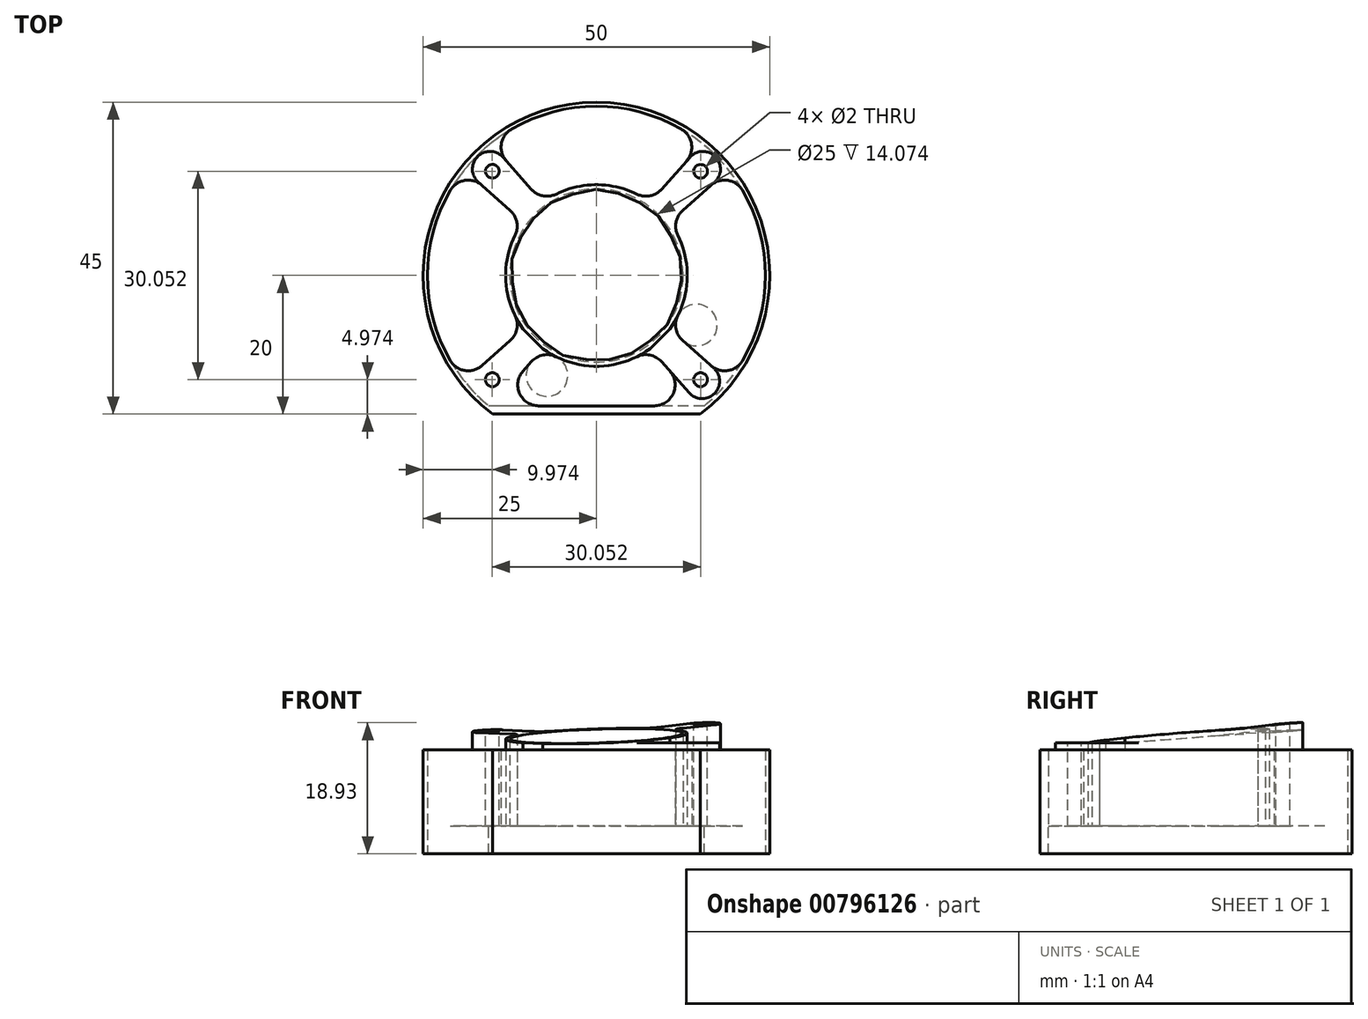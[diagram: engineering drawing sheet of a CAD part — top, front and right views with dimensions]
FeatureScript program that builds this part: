
annotation { "Feature Type Name" : "Feature", "Feature Type Description" : "" }
export const myFeature = defineFeature(function(context is Context, id is Id, definition is map)
    precondition{}
    {
        {
            var Q0;
            Q0=qCreatedBy(makeId("Top.planeOp"),FACE);
            var sketch = newSketch(context, id + "F0", { "sketchPlane" : qUnion([Q0])});
            skLineSegment(sketch, "E0", {"start": v(0, 25) * mm, "end": v(0, -20) * mm, "construction": true});
            skLineSegment(sketch, "E1", {"start": v(0, -20) * mm, "end": v(-15, -20) * mm});
            skLineSegment(sketch, "E2", {"start": v(0, -20) * mm, "end": v(15, -20) * mm});
            skArc(sketch, "E3", {"start": v(-15, -20) * mm, "mid": v(0, -25) * mm, "end": v(15, -20) * mm, "construction": true});
            skArc(sketch, "E4", {"start": v(15, -20) * mm, "mid": v(0, 25) * mm, "end": v(-15, -20) * mm});
            skCircle(sketch, "E5", {"center": v(0, 0) * mm, "radius": 12.5 * mm});
            skCircle(sketch, "E6", {"center": v(0, 0) * mm, "radius": 13.1 * mm});
            skArc(sketch, "E7", {"start": v(13.98, -20) * mm, "mid": v(0, 24.4) * mm, "end": v(-13.98, -20) * mm});
            skArc(sketch, "E8", {"start": v(-13.98, -20) * mm, "mid": v(0, -24.4) * mm, "end": v(13.98, -20) * mm, "construction": true});
            skLineSegment(sketch, "E9", {"start": v(0, -20) * mm, "end": v(0, -18.8) * mm});
            skLineSegment(sketch, "E10", {"start": v(0, -18.8) * mm, "end": v(-15.55, -18.8) * mm});
            skLineSegment(sketch, "E11", {"start": v(0, -18.8) * mm, "end": v(15.55, -18.8) * mm});
            skSolve(sketch);
        }
        {
            var Q0;
            {var subQ0=sQuery(id+"F0.wireOp",EDGE,"E4");Q0=makeQuery(id+"F0.imprint","IMPRINT",FACE,{"disambiguationData":[TD([[makeQuery(id+"F0.imprint","IMPRINT",EDGE,{"derivedFrom":subQ0}),1.0]])]});}
            var Q1;
            Q1=makeQuery(id+"F0.imprint","IMPRINT",FACE,{"disambiguationData":[TD([[makeQuery(id+"F0.imprint","IMPRINT",EDGE,{"derivedFrom":sQuery(id+"F0.wireOp",EDGE,"E5")}),-1.0]])]});
            var Q2;
            {var subQ0=sQuery(id+"F0.wireOp",EDGE,"E9");Q2=makeQuery(id+"F0.imprint","IMPRINT",FACE,{"disambiguationData":[TD([[makeQuery(id+"F0.imprint","IMPRINT",EDGE,{"derivedFrom":subQ0}),1.0]])]});}
            var Q3;
            {var subQ0=sQuery(id+"F0.wireOp",EDGE,"E9");Q3=makeQuery(id+"F0.imprint","IMPRINT",FACE,{"disambiguationData":[TD([[makeQuery(id+"F0.imprint","IMPRINT",EDGE,{"derivedFrom":subQ0}),-1.0]])]});}
            extrude(context, id + "F1", {"entities" : qUnion([Q0, Q1, Q2, Q3]), "depth" : 8 * mm, "offsetDistance" : 25 * mm});
        }
        {
            var Q0;
            Q0=makeQuery(id+"F1.opExtrude","CAP_FACE",FACE,{"disambiguationData":[OSD([sQuery(id+"F0.wireOp",EDGE,"E1"),sQuery(id+"F0.wireOp",EDGE,"E2"),sQuery(id+"F0.wireOp",EDGE,"E4"),sQuery(id+"F0.wireOp",EDGE,"E7"),sQuery(id+"F0.wireOp",EDGE,"E10"),sQuery(id+"F0.wireOp",EDGE,"E11")])],"isStart":false});
            var sketch = newSketch(context, id + "F2", { "sketchPlane" : qUnion([Q0])});
            skCircle(sketch, "E12", {"center": v(0, 0) * mm, "radius": 21.25 * mm, "construction": true});
            skLineSegment(sketch, "E13", {"start": v(0, 0) * mm, "end": v(0, 21.25) * mm, "construction": true});
            skLineSegment(sketch, "E14", {"start": v(0, 0) * mm, "end": v(15.03, 15.03) * mm, "construction": true});
            skCircle(sketch, "E15", {"center": v(15.03, 15.03) * mm, "radius": 1 * mm});
            skCircle(sketch, "E16", {"center": v(15.03, 15.03) * mm, "radius": 2.5 * mm});
            skLineSegment(sketch, "E17", {"start": v(13.16, 16.69) * mm, "end": v(7.73, 10.58) * mm});
            skLineSegment(sketch, "E18", {"start": v(16.69, 13.16) * mm, "end": v(10.58, 7.73) * mm});
            skLineSegment(sketch, "E19", {"start": v(13.16, 16.69) * mm, "end": v(15.25, 19.04) * mm});
            skLineSegment(sketch, "E20", {"start": v(16.69, 13.16) * mm, "end": v(19.04, 15.25) * mm});
            skLineSegment(sketch, "E21", {"start": v(7.73, 10.58) * mm, "end": v(10.58, 7.73) * mm});
            skSolve(sketch);
        }
        {
            var Q0;
            Q0=makeQuery(id+"F2.imprint","IMPRINT",FACE,{"disambiguationData":[TD([[makeQuery(id+"F2.imprint","IMPRINT",EDGE,{"derivedFrom":sQuery(id+"F2.wireOp",EDGE,"E15")}),-1.0]])]});
            var Q1;
            {var subQ0=sQuery(id+"F2.wireOp",EDGE,"E19");Q1=makeQuery(id+"F2.imprint","IMPRINT",FACE,{"disambiguationData":[TD([[makeQuery(id+"F2.imprint","IMPRINT",EDGE,{"derivedFrom":subQ0}),-1.0]])]});}
            var Q2;
            {var subQ0=sQuery(id+"F2.wireOp",EDGE,"E17");Q2=makeQuery(id+"F2.imprint","IMPRINT",FACE,{"disambiguationData":[TD([[makeQuery(id+"F2.imprint","IMPRINT",EDGE,{"derivedFrom":subQ0}),1.0]])]});}
            extrude(context, id + "F3", {"entities" : qUnion([Q0, Q1, Q2]), "oppositeDirection" : true, "depth" : 8 * mm, "offsetDistance" : 25 * mm});
        }
        {
            var Q0;
            Q0=makeQuery(id+"F3.opExtrude","SWEPT_BODY",BODY,{"disambiguationData":[OSD([sQuery(id+"F0.wireOp",EDGE,"E7"),sQuery(id+"F2.wireOp",EDGE,"E15"),sQuery(id+"F2.wireOp",EDGE,"E17"),sQuery(id+"F2.wireOp",EDGE,"E18"),sQuery(id+"F2.wireOp",EDGE,"E19"),sQuery(id+"F2.wireOp",EDGE,"E20"),sQuery(id+"F2.wireOp",EDGE,"E21")])]});
            var Q1;
            Q1=makeQuery(id+"F1.opExtrude","CAP_EDGE",EDGE,{"disambiguationData":[OSD([sQuery(id+"F0.wireOp",EDGE,"E6")])],"isStart":false});
            circularPattern(context, id + "F4", {"entities" : qUnion([Q0]), "axis" : qUnion([Q1]), "angle" : 360 * degree, "instanceCount" : 4, "equalSpace" : true});
        }
        {
            var Q0;
            Q0=makeQuery(id+"F1.opExtrude","CAP_FACE",FACE,{"disambiguationData":[OSD([sQuery(id+"F0.wireOp",EDGE,"E1"),sQuery(id+"F0.wireOp",EDGE,"E2"),sQuery(id+"F0.wireOp",EDGE,"E4"),sQuery(id+"F0.wireOp",EDGE,"E7"),sQuery(id+"F0.wireOp",EDGE,"E10"),sQuery(id+"F0.wireOp",EDGE,"E11")])],"isStart":true});
            extrude(context, id + "F5", {"entities" : qUnion([Q0]), "operationType" : NewBodyOperationType.ADD, "depth" : 4 * mm, "offsetDistance" : 25 * mm});
        }
        {
            var Q0;
            Q0=makeQuery(id+"F1.opExtrude","SWEPT_BODY",BODY,{"disambiguationData":[OSD([sQuery(id+"F0.wireOp",EDGE,"E1"),sQuery(id+"F0.wireOp",EDGE,"E2"),sQuery(id+"F0.wireOp",EDGE,"E4"),sQuery(id+"F0.wireOp",EDGE,"E7"),sQuery(id+"F0.wireOp",EDGE,"E10"),sQuery(id+"F0.wireOp",EDGE,"E11")])]});
            var Q1;
            Q1=makeQuery(id+"F1.opExtrude","SWEPT_BODY",BODY,{"disambiguationData":[OSD([sQuery(id+"F0.wireOp",EDGE,"E5"),sQuery(id+"F0.wireOp",EDGE,"E6")])]});
            booleanBodies(context, id + "F6", {"operationType" : BooleanOperationType.UNION, "tools" : qUnion([Q0, Q1])});
        }
        {
            var Q0;
            {var subQ0=sQuery(id+"F0.wireOp",EDGE,"E7");var subQ1=makeQuery(id+"F3.opExtrude","CAP_FACE",FACE,{"disambiguationData":[OSD([subQ0,sQuery(id+"F2.wireOp",EDGE,"E15"),sQuery(id+"F2.wireOp",EDGE,"E17"),sQuery(id+"F2.wireOp",EDGE,"E18"),sQuery(id+"F2.wireOp",EDGE,"E19"),sQuery(id+"F2.wireOp",EDGE,"E20"),sQuery(id+"F2.wireOp",EDGE,"E21")])],"isStart":true});Q0=makeQuery(id+"F6.opBoolean","MERGE",FACE,{"derivedFrom":[makeQuery(id+"F1.opExtrude","CAP_FACE",FACE,{"disambiguationData":[OSD([sQuery(id+"F0.wireOp",EDGE,"E5"),sQuery(id+"F0.wireOp",EDGE,"E6")])],"isStart":false}),makeQuery(id+"F5.boolean.opBoolean","MERGE",FACE,{"derivedFrom":[makeQuery(id+"F1.opExtrude","CAP_FACE",FACE,{"disambiguationData":[OSD([sQuery(id+"F0.wireOp",EDGE,"E1"),sQuery(id+"F0.wireOp",EDGE,"E2"),sQuery(id+"F0.wireOp",EDGE,"E4"),subQ0,sQuery(id+"F0.wireOp",EDGE,"E10"),sQuery(id+"F0.wireOp",EDGE,"E11")])],"isStart":false}),subQ1,makeQuery(id+"F4.opPattern","COPY",FACE,{"derivedFrom":subQ1,"instanceName":"1"}),makeQuery(id+"F4.opPattern","COPY",FACE,{"derivedFrom":subQ1,"instanceName":"2"}),makeQuery(id+"F4.opPattern","COPY",FACE,{"derivedFrom":subQ1,"instanceName":"3"})]})]});}
            var sketch = newSketch(context, id + "F7", { "sketchPlane" : qUnion([Q0])});
            skLineSegment(sketch, "E22", {"start": v(15.25, 19.04) * mm, "end": v(19.04, 15.25) * mm});
            skLineSegment(sketch, "E23", {"start": v(19.04, 15.25) * mm, "end": v(10.58, 7.73) * mm});
            skLineSegment(sketch, "E24", {"start": v(10.58, 7.73) * mm, "end": v(7.73, 10.58) * mm});
            skLineSegment(sketch, "E25", {"start": v(7.73, 10.58) * mm, "end": v(15.25, 19.04) * mm});
            skCircle(sketch, "E26", {"center": v(15.03, 15.03) * mm, "radius": 2.5 * mm});
            skSolve(sketch);
        }
        {
            var Q0;
            {var subQ0=sQuery(id+"F7.wireOp",EDGE,"E24");Q0=makeQuery(id+"F7.imprint","IMPRINT",FACE,{"disambiguationData":[TD([[makeQuery(id+"F7.imprint","IMPRINT",EDGE,{"derivedFrom":subQ0}),-1.0]])]});}
            var Q1;
            {var subQ0=sQuery(id+"F7.wireOp",EDGE,"E22");Q1=makeQuery(id+"F7.imprint","IMPRINT",FACE,{"disambiguationData":[TD([[makeQuery(id+"F7.imprint","IMPRINT",EDGE,{"derivedFrom":subQ0}),-1.0]])]});}
            var Q2;
            Q2=makeQuery(id+"F7.imprint","IMPRINT",FACE,{"disambiguationData":[TD([[makeQuery(id+"F7.imprint","IMPRINT",EDGE,{"derivedFrom":makeQuery(id+"F3.opExtrude","CAP_EDGE",EDGE,{"disambiguationData":[OSD([sQuery(id+"F2.wireOp",EDGE,"E15")])],"isStart":true})}),-1.0]])]});
            extrude(context, id + "F8", {"entities" : qUnion([Q0, Q1, Q2]), "operationType" : NewBodyOperationType.ADD, "depth" : 7 * mm, "offsetDistance" : 25 * mm});
        }
        {
            var Q0;
            {var subQ0=sQuery(id+"F0.wireOp",EDGE,"E7");var subQ1=makeQuery(id+"F3.opExtrude","CAP_FACE",FACE,{"disambiguationData":[OSD([subQ0,sQuery(id+"F2.wireOp",EDGE,"E15"),sQuery(id+"F2.wireOp",EDGE,"E17"),sQuery(id+"F2.wireOp",EDGE,"E18"),sQuery(id+"F2.wireOp",EDGE,"E19"),sQuery(id+"F2.wireOp",EDGE,"E20"),sQuery(id+"F2.wireOp",EDGE,"E21")])],"isStart":true});Q0=makeQuery(id+"F6.opBoolean","MERGE",FACE,{"derivedFrom":[makeQuery(id+"F1.opExtrude","CAP_FACE",FACE,{"disambiguationData":[OSD([sQuery(id+"F0.wireOp",EDGE,"E5"),sQuery(id+"F0.wireOp",EDGE,"E6")])],"isStart":false}),makeQuery(id+"F5.boolean.opBoolean","MERGE",FACE,{"derivedFrom":[makeQuery(id+"F1.opExtrude","CAP_FACE",FACE,{"disambiguationData":[OSD([sQuery(id+"F0.wireOp",EDGE,"E1"),sQuery(id+"F0.wireOp",EDGE,"E2"),sQuery(id+"F0.wireOp",EDGE,"E4"),subQ0,sQuery(id+"F0.wireOp",EDGE,"E10"),sQuery(id+"F0.wireOp",EDGE,"E11")])],"isStart":false}),subQ1,makeQuery(id+"F4.opPattern","COPY",FACE,{"derivedFrom":subQ1,"instanceName":"1"}),makeQuery(id+"F4.opPattern","COPY",FACE,{"derivedFrom":subQ1,"instanceName":"2"}),makeQuery(id+"F4.opPattern","COPY",FACE,{"derivedFrom":subQ1,"instanceName":"3"})]})]});}
            var sketch = newSketch(context, id + "F9", { "sketchPlane" : qUnion([Q0])});
            skLineSegment(sketch, "E27", {"start": v(-15.25, 19.04) * mm, "end": v(-19.04, 15.25) * mm});
            skLineSegment(sketch, "E28", {"start": v(-19.04, 15.25) * mm, "end": v(-10.58, 7.73) * mm});
            skLineSegment(sketch, "E29", {"start": v(-10.58, 7.73) * mm, "end": v(-7.73, 10.58) * mm});
            skLineSegment(sketch, "E30", {"start": v(-7.73, 10.58) * mm, "end": v(-15.25, 19.04) * mm});
            skSolve(sketch);
        }
        {
            var Q0;
            Q0=makeQuery(id+"F9.imprint","IMPRINT",FACE,{"disambiguationData":[TD([[makeQuery(id+"F9.imprint","IMPRINT",EDGE,{"derivedFrom":sQuery(id+"F9.wireOp",EDGE,"E27")}),1.0]])]});
            extrude(context, id + "F10", {"entities" : qUnion([Q0]), "operationType" : NewBodyOperationType.ADD, "depth" : 6 * mm, "offsetDistance" : 25 * mm});
        }
        {
            var Q0;
            {var subQ0=sQuery(id+"F0.wireOp",EDGE,"E7");var subQ1=makeQuery(id+"F3.opExtrude","CAP_FACE",FACE,{"disambiguationData":[OSD([subQ0,sQuery(id+"F2.wireOp",EDGE,"E15"),sQuery(id+"F2.wireOp",EDGE,"E17"),sQuery(id+"F2.wireOp",EDGE,"E18"),sQuery(id+"F2.wireOp",EDGE,"E19"),sQuery(id+"F2.wireOp",EDGE,"E20"),sQuery(id+"F2.wireOp",EDGE,"E21")])],"isStart":true});Q0=makeQuery(id+"F6.opBoolean","MERGE",FACE,{"derivedFrom":[makeQuery(id+"F1.opExtrude","CAP_FACE",FACE,{"disambiguationData":[OSD([sQuery(id+"F0.wireOp",EDGE,"E5"),sQuery(id+"F0.wireOp",EDGE,"E6")])],"isStart":false}),makeQuery(id+"F5.boolean.opBoolean","MERGE",FACE,{"derivedFrom":[makeQuery(id+"F1.opExtrude","CAP_FACE",FACE,{"disambiguationData":[OSD([sQuery(id+"F0.wireOp",EDGE,"E1"),sQuery(id+"F0.wireOp",EDGE,"E2"),sQuery(id+"F0.wireOp",EDGE,"E4"),subQ0,sQuery(id+"F0.wireOp",EDGE,"E10"),sQuery(id+"F0.wireOp",EDGE,"E11")])],"isStart":false}),subQ1,makeQuery(id+"F4.opPattern","COPY",FACE,{"derivedFrom":subQ1,"instanceName":"1"}),makeQuery(id+"F4.opPattern","COPY",FACE,{"derivedFrom":subQ1,"instanceName":"2"}),makeQuery(id+"F4.opPattern","COPY",FACE,{"derivedFrom":subQ1,"instanceName":"3"})]})]});}
            var sketch = newSketch(context, id + "F11", { "sketchPlane" : qUnion([Q0])});
            skLineSegment(sketch, "E31", {"start": v(-19.04, -15.25) * mm, "end": v(-15.04, -18.8) * mm});
            skLineSegment(sketch, "E32", {"start": v(-15.04, -18.8) * mm, "end": v(-7.73, -10.58) * mm});
            skLineSegment(sketch, "E33", {"start": v(-7.73, -10.58) * mm, "end": v(-10.58, -7.73) * mm});
            skSolve(sketch);
        }
        {
            var Q0;
            Q0=makeQuery(id+"F11.imprint","IMPRINT",FACE,{"disambiguationData":[TD([[makeQuery(id+"F11.imprint","IMPRINT",EDGE,{"derivedFrom":sQuery(id+"F11.wireOp",EDGE,"E31")}),1.0]])]});
            extrude(context, id + "F12", {"entities" : qUnion([Q0]), "operationType" : NewBodyOperationType.ADD, "depth" : 3 * mm, "offsetDistance" : 25 * mm});
        }
        {
            var Q0;
            {var subQ0=sQuery(id+"F0.wireOp",EDGE,"E7");var subQ1=makeQuery(id+"F3.opExtrude","CAP_FACE",FACE,{"disambiguationData":[OSD([subQ0,sQuery(id+"F2.wireOp",EDGE,"E15"),sQuery(id+"F2.wireOp",EDGE,"E17"),sQuery(id+"F2.wireOp",EDGE,"E18"),sQuery(id+"F2.wireOp",EDGE,"E19"),sQuery(id+"F2.wireOp",EDGE,"E20"),sQuery(id+"F2.wireOp",EDGE,"E21")])],"isStart":true});Q0=makeQuery(id+"F6.opBoolean","MERGE",FACE,{"derivedFrom":[makeQuery(id+"F1.opExtrude","CAP_FACE",FACE,{"disambiguationData":[OSD([sQuery(id+"F0.wireOp",EDGE,"E5"),sQuery(id+"F0.wireOp",EDGE,"E6")])],"isStart":false}),makeQuery(id+"F5.boolean.opBoolean","MERGE",FACE,{"derivedFrom":[makeQuery(id+"F1.opExtrude","CAP_FACE",FACE,{"disambiguationData":[OSD([sQuery(id+"F0.wireOp",EDGE,"E1"),sQuery(id+"F0.wireOp",EDGE,"E2"),sQuery(id+"F0.wireOp",EDGE,"E4"),subQ0,sQuery(id+"F0.wireOp",EDGE,"E10"),sQuery(id+"F0.wireOp",EDGE,"E11")])],"isStart":false}),subQ1,makeQuery(id+"F4.opPattern","COPY",FACE,{"derivedFrom":subQ1,"instanceName":"1"}),makeQuery(id+"F4.opPattern","COPY",FACE,{"derivedFrom":subQ1,"instanceName":"2"}),makeQuery(id+"F4.opPattern","COPY",FACE,{"derivedFrom":subQ1,"instanceName":"3"})]})]});}
            var sketch = newSketch(context, id + "F13", { "sketchPlane" : qUnion([Q0])});
            skLineSegment(sketch, "E34", {"start": v(7.73, -10.58) * mm, "end": v(10.58, -7.73) * mm});
            skLineSegment(sketch, "E35", {"start": v(10.58, -7.73) * mm, "end": v(19.04, -15.25) * mm});
            skLineSegment(sketch, "E36", {"start": v(19.04, -15.25) * mm, "end": v(15.04, -18.8) * mm});
            skLineSegment(sketch, "E37", {"start": v(15.04, -18.8) * mm, "end": v(7.73, -10.58) * mm});
            skSolve(sketch);
        }
        {
            var Q0;
            Q0=makeQuery(id+"F13.imprint","IMPRINT",FACE,{"disambiguationData":[TD([[makeQuery(id+"F13.imprint","IMPRINT",EDGE,{"derivedFrom":sQuery(id+"F13.wireOp",EDGE,"E34")}),-1.0]])]});
            extrude(context, id + "F14", {"entities" : qUnion([Q0]), "operationType" : NewBodyOperationType.ADD, "depth" : 4 * mm, "offsetDistance" : 25 * mm});
        }
        {
            var Q0;
            {var subQ0=sQuery(id+"F2.wireOp",EDGE,"E20");var subQ1=sQuery(id+"F2.wireOp",EDGE,"E18");var subQ3=sQuery(id+"F2.wireOp",EDGE,"E19");var subQ4=sQuery(id+"F2.wireOp",EDGE,"E17");var subQ6=sQuery(id+"F0.wireOp",EDGE,"E6");var subQ7=sQuery(id+"F0.wireOp",EDGE,"E5");var subQ8=sQuery(id+"F0.wireOp",EDGE,"E7");var subQ9=makeQuery(id+"F3.opExtrude","CAP_FACE",FACE,{"disambiguationData":[OSD([subQ8,sQuery(id+"F2.wireOp",EDGE,"E15"),subQ4,subQ1,subQ3,subQ0,sQuery(id+"F2.wireOp",EDGE,"E21")])],"isStart":true});Q0=makeQuery(id+"F14.boolean.opBoolean","SPLIT",FACE,{"disambiguationData":[TD([makeQuery(id+"F1.opExtrude","SWEPT_FACE",FACE,{"disambiguationData":[OSD([subQ7])]})])],"derivedFrom":makeQuery(id+"F6.opBoolean","MERGE",FACE,{"derivedFrom":[makeQuery(id+"F1.opExtrude","CAP_FACE",FACE,{"disambiguationData":[OSD([subQ7,subQ6])],"isStart":false}),makeQuery(id+"F5.boolean.opBoolean","MERGE",FACE,{"derivedFrom":[makeQuery(id+"F1.opExtrude","CAP_FACE",FACE,{"disambiguationData":[OSD([sQuery(id+"F0.wireOp",EDGE,"E1"),sQuery(id+"F0.wireOp",EDGE,"E2"),sQuery(id+"F0.wireOp",EDGE,"E4"),subQ8,sQuery(id+"F0.wireOp",EDGE,"E10"),sQuery(id+"F0.wireOp",EDGE,"E11")])],"isStart":false}),subQ9,makeQuery(id+"F4.opPattern","COPY",FACE,{"derivedFrom":subQ9,"instanceName":"1"}),makeQuery(id+"F4.opPattern","COPY",FACE,{"derivedFrom":subQ9,"instanceName":"2"}),makeQuery(id+"F4.opPattern","COPY",FACE,{"derivedFrom":subQ9,"instanceName":"3"})]})]})});}
            extrude(context, id + "F15", {"entities" : qUnion([Q0]), "operationType" : NewBodyOperationType.ADD, "depth" : 7 * mm, "offsetDistance" : 25 * mm});
        }
        {
            var Q0;
            Q0=makeQuery(id+"F8.opExtrude","CAP_VERTEX",VERTEX,{"disambiguationData":[OSD([sQuery(id+"F0.wireOp",EDGE,"E7"),sQuery(id+"F7.wireOp",EDGE,"E22"),sQuery(id+"F7.wireOp",EDGE,"E25")])],"isStart":false});
            var Q1;
            Q1=makeQuery(id+"F14.opExtrude","CAP_VERTEX",VERTEX,{"disambiguationData":[OSD([sQuery(id+"F0.wireOp",EDGE,"E10"),sQuery(id+"F0.wireOp",EDGE,"E11"),sQuery(id+"F13.wireOp",EDGE,"E36"),sQuery(id+"F13.wireOp",EDGE,"E37")])],"isStart":false});
            var Q2;
            Q2=makeQuery(id+"F12.opExtrude","CAP_VERTEX",VERTEX,{"disambiguationData":[OSD([sQuery(id+"F0.wireOp",EDGE,"E10"),sQuery(id+"F0.wireOp",EDGE,"E11"),sQuery(id+"F11.wireOp",EDGE,"E31"),sQuery(id+"F11.wireOp",EDGE,"E32")])],"isStart":false});
            cPlane(context, id + "F16", {"entities" : qUnion([Q0, Q1, Q2]), "cplaneType" : CPlaneType.THREE_POINT, "offset" : 25 * mm, "width" : 150 * mm, "height" : 150 * mm});
        }
        {
            var Q0;
            Q0=qCreatedBy(id+"F16.planeOp",FACE);
            var sketch = newSketch(context, id + "F17", { "sketchPlane" : qUnion([Q0])});
            skLineSegment(sketch, "E38.bottom", {"start": v(-22.72, -24.84) * mm, "end": v(31.37, -24.84) * mm});
            skLineSegment(sketch, "E38.top", {"start": v(-22.72, 19.98) * mm, "end": v(31.37, 19.98) * mm});
            skLineSegment(sketch, "E38.left", {"start": v(-22.72, -24.84) * mm, "end": v(-22.72, 19.98) * mm});
            skLineSegment(sketch, "E38.right", {"start": v(31.37, -24.84) * mm, "end": v(31.37, 19.98) * mm});
            skSolve(sketch);
        }
        {
            var Q0;
            Q0=makeQuery(id+"F17.imprint","IMPRINT",FACE,{"disambiguationData":[TD([[makeQuery(id+"F17.imprint","IMPRINT",EDGE,{"derivedFrom":sQuery(id+"F17.wireOp",EDGE,"E38.bottom")}),1.0]])]});
            extrude(context, id + "F18", {"entities" : qUnion([Q0]), "operationType" : NewBodyOperationType.REMOVE, "depth" : 25 * mm, "offsetDistance" : 25 * mm});
        }
        {
            var Q0;
            {var subQ0=sQuery(id+"F2.wireOp",EDGE,"E20");var subQ1=sQuery(id+"F2.wireOp",EDGE,"E18");var subQ3=sQuery(id+"F0.wireOp",EDGE,"E11");var subQ4=sQuery(id+"F0.wireOp",EDGE,"E10");var subQ5=sQuery(id+"F0.wireOp",EDGE,"E2");var subQ6=sQuery(id+"F0.wireOp",EDGE,"E1");var subQ7=sQuery(id+"F2.wireOp",EDGE,"E19");var subQ8=sQuery(id+"F2.wireOp",EDGE,"E17");var subQ10=sQuery(id+"F0.wireOp",EDGE,"E4");var subQ11=sQuery(id+"F0.wireOp",EDGE,"E7");var subQ12=makeQuery(id+"F3.opExtrude","CAP_FACE",FACE,{"disambiguationData":[OSD([subQ11,sQuery(id+"F2.wireOp",EDGE,"E15"),subQ8,subQ1,subQ7,subQ0,sQuery(id+"F2.wireOp",EDGE,"E21")])],"isStart":true});Q0=makeQuery(id+"F14.boolean.opBoolean","SPLIT",FACE,{"disambiguationData":[TD([makeQuery(id+"F1.opExtrude","SWEPT_FACE",FACE,{"disambiguationData":[OSD([subQ10])]})])],"derivedFrom":makeQuery(id+"F6.opBoolean","MERGE",FACE,{"derivedFrom":[makeQuery(id+"F1.opExtrude","CAP_FACE",FACE,{"disambiguationData":[OSD([sQuery(id+"F0.wireOp",EDGE,"E5"),sQuery(id+"F0.wireOp",EDGE,"E6")])],"isStart":false}),makeQuery(id+"F5.boolean.opBoolean","MERGE",FACE,{"derivedFrom":[makeQuery(id+"F1.opExtrude","CAP_FACE",FACE,{"disambiguationData":[OSD([subQ6,subQ5,subQ10,subQ11,subQ4,subQ3])],"isStart":false}),subQ12,makeQuery(id+"F4.opPattern","COPY",FACE,{"derivedFrom":subQ12,"instanceName":"1"}),makeQuery(id+"F4.opPattern","COPY",FACE,{"derivedFrom":subQ12,"instanceName":"2"}),makeQuery(id+"F4.opPattern","COPY",FACE,{"derivedFrom":subQ12,"instanceName":"3"})]})]})});}
            extrude(context, id + "F19", {"entities" : qUnion([Q0]), "operationType" : NewBodyOperationType.ADD, "depth" : 3 * mm, "offsetDistance" : 25 * mm});
        }
        {
            var Q0;
            {var subQ0=sQuery(id+"F11.wireOp",EDGE,"E31");var subQ1=sQuery(id+"F2.wireOp",EDGE,"E20");var subQ2=sQuery(id+"F2.wireOp",EDGE,"E18");var subQ3=sQuery(id+"F0.wireOp",EDGE,"E7");Q0=makeQuery(id+"F19.boolean.opBoolean","MERGE",EDGE,{"derivedFrom":[makeQuery(id+"F4.opPattern","COPY",EDGE,{"derivedFrom":makeQuery(id+"F3.opExtrude","SWEPT_EDGE",EDGE,{"disambiguationData":[OSD([subQ3,subQ1])]}),"instanceName":"2"}),makeQuery(id+"F12.opExtrude","SWEPT_EDGE",EDGE,{"disambiguationData":[OSD([subQ3,subQ2,subQ1,subQ0])]}),makeQuery(id+"F19.opExtrude","SWEPT_EDGE",EDGE,{"disambiguationData":[OSD([subQ3,subQ2,subQ1,subQ0])]})]});}
            var Q1;
            {var subQ0=sQuery(id+"F11.wireOp",EDGE,"E33");var subQ1=sQuery(id+"F2.wireOp",EDGE,"E21");var subQ2=sQuery(id+"F2.wireOp",EDGE,"E20");var subQ3=sQuery(id+"F2.wireOp",EDGE,"E18");var subQ4=sQuery(id+"F0.wireOp",EDGE,"E6");Q1=makeQuery(id+"F15.boolean.opBoolean","MERGE",EDGE,{"derivedFrom":[makeQuery(id+"F4.opPattern","COPY",EDGE,{"derivedFrom":makeQuery(id+"F3.opExtrude","SWEPT_EDGE",EDGE,{"disambiguationData":[OSD([subQ3,subQ1])]}),"instanceName":"2"}),makeQuery(id+"F12.opExtrude","SWEPT_EDGE",EDGE,{"disambiguationData":[OSD([subQ4,subQ3,subQ2,subQ0])]}),makeQuery(id+"F15.opExtrude","SWEPT_EDGE",EDGE,{"disambiguationData":[OSD([subQ4,subQ3,subQ2,subQ1,subQ0])]})]});}
            var Q2;
            {var subQ0=sQuery(id+"F11.wireOp",EDGE,"E33");var subQ1=sQuery(id+"F11.wireOp",EDGE,"E32");var subQ2=sQuery(id+"F2.wireOp",EDGE,"E21");var subQ3=sQuery(id+"F2.wireOp",EDGE,"E17");var subQ4=sQuery(id+"F0.wireOp",EDGE,"E6");Q2=makeQuery(id+"F15.boolean.opBoolean","MERGE",EDGE,{"derivedFrom":[makeQuery(id+"F4.opPattern","COPY",EDGE,{"derivedFrom":makeQuery(id+"F3.opExtrude","SWEPT_EDGE",EDGE,{"disambiguationData":[OSD([subQ3,subQ2])]}),"instanceName":"2"}),makeQuery(id+"F12.opExtrude","SWEPT_EDGE",EDGE,{"disambiguationData":[OSD([subQ4,subQ1,subQ0])]}),makeQuery(id+"F15.opExtrude","SWEPT_EDGE",EDGE,{"disambiguationData":[OSD([subQ4,subQ3,subQ2,subQ1,subQ0])]})]});}
            var Q3;
            {var subQ0=sQuery(id+"F9.wireOp",EDGE,"E29");var subQ1=sQuery(id+"F9.wireOp",EDGE,"E28");var subQ2=sQuery(id+"F2.wireOp",EDGE,"E21");var subQ3=sQuery(id+"F2.wireOp",EDGE,"E17");var subQ4=sQuery(id+"F0.wireOp",EDGE,"E6");Q3=makeQuery(id+"F15.boolean.opBoolean","MERGE",EDGE,{"derivedFrom":[makeQuery(id+"F4.opPattern","COPY",EDGE,{"derivedFrom":makeQuery(id+"F3.opExtrude","SWEPT_EDGE",EDGE,{"disambiguationData":[OSD([subQ3,subQ2])]}),"instanceName":"1"}),makeQuery(id+"F10.opExtrude","SWEPT_EDGE",EDGE,{"disambiguationData":[OSD([subQ4,subQ1,subQ0])]}),makeQuery(id+"F15.opExtrude","SWEPT_EDGE",EDGE,{"disambiguationData":[OSD([subQ4,subQ3,subQ2,subQ1,subQ0])]})]});}
            var Q4;
            {var subQ0=sQuery(id+"F9.wireOp",EDGE,"E28");var subQ1=sQuery(id+"F9.wireOp",EDGE,"E27");var subQ2=sQuery(id+"F2.wireOp",EDGE,"E19");var subQ3=sQuery(id+"F0.wireOp",EDGE,"E7");Q4=makeQuery(id+"F19.boolean.opBoolean","MERGE",EDGE,{"derivedFrom":[makeQuery(id+"F4.opPattern","COPY",EDGE,{"derivedFrom":makeQuery(id+"F3.opExtrude","SWEPT_EDGE",EDGE,{"disambiguationData":[OSD([subQ3,subQ2])]}),"instanceName":"1"}),makeQuery(id+"F10.opExtrude","SWEPT_EDGE",EDGE,{"disambiguationData":[OSD([subQ3,subQ1,subQ0])]}),makeQuery(id+"F19.opExtrude","SWEPT_EDGE",EDGE,{"disambiguationData":[OSD([subQ3,subQ2,subQ1,subQ0])]})]});}
            var Q5;
            {var subQ0=sQuery(id+"F9.wireOp",EDGE,"E30");var subQ1=sQuery(id+"F9.wireOp",EDGE,"E27");var subQ2=sQuery(id+"F2.wireOp",EDGE,"E20");var subQ3=sQuery(id+"F0.wireOp",EDGE,"E7");Q5=makeQuery(id+"F19.boolean.opBoolean","MERGE",EDGE,{"derivedFrom":[makeQuery(id+"F4.opPattern","COPY",EDGE,{"derivedFrom":makeQuery(id+"F3.opExtrude","SWEPT_EDGE",EDGE,{"disambiguationData":[OSD([subQ3,subQ2])]}),"instanceName":"1"}),makeQuery(id+"F10.opExtrude","SWEPT_EDGE",EDGE,{"disambiguationData":[OSD([subQ3,subQ1,subQ0])]}),makeQuery(id+"F19.opExtrude","SWEPT_EDGE",EDGE,{"disambiguationData":[OSD([subQ3,subQ2,subQ1,subQ0])]})]});}
            var Q6;
            {var subQ0=sQuery(id+"F9.wireOp",EDGE,"E30");var subQ1=sQuery(id+"F9.wireOp",EDGE,"E29");var subQ2=sQuery(id+"F2.wireOp",EDGE,"E21");var subQ3=sQuery(id+"F2.wireOp",EDGE,"E18");var subQ4=sQuery(id+"F0.wireOp",EDGE,"E6");Q6=makeQuery(id+"F15.boolean.opBoolean","MERGE",EDGE,{"derivedFrom":[makeQuery(id+"F4.opPattern","COPY",EDGE,{"derivedFrom":makeQuery(id+"F3.opExtrude","SWEPT_EDGE",EDGE,{"disambiguationData":[OSD([subQ3,subQ2])]}),"instanceName":"1"}),makeQuery(id+"F10.opExtrude","SWEPT_EDGE",EDGE,{"disambiguationData":[OSD([subQ4,subQ1,subQ0])]}),makeQuery(id+"F15.opExtrude","SWEPT_EDGE",EDGE,{"disambiguationData":[OSD([subQ4,subQ3,subQ2,subQ1,subQ0])]})]});}
            var Q7;
            {var subQ0=sQuery(id+"F7.wireOp",EDGE,"E25");var subQ1=sQuery(id+"F7.wireOp",EDGE,"E22");var subQ2=sQuery(id+"F2.wireOp",EDGE,"E19");var subQ3=sQuery(id+"F0.wireOp",EDGE,"E7");Q7=makeQuery(id+"F19.boolean.opBoolean","MERGE",EDGE,{"derivedFrom":[makeQuery(id+"F3.opExtrude","SWEPT_EDGE",EDGE,{"disambiguationData":[OSD([subQ3,subQ2])]}),makeQuery(id+"F8.opExtrude","SWEPT_EDGE",EDGE,{"disambiguationData":[OSD([subQ3,subQ1,subQ0])]}),makeQuery(id+"F19.opExtrude","SWEPT_EDGE",EDGE,{"disambiguationData":[OSD([subQ3,subQ2,subQ1,subQ0])]})]});}
            var Q8;
            {var subQ0=sQuery(id+"F7.wireOp",EDGE,"E25");var subQ1=sQuery(id+"F7.wireOp",EDGE,"E24");var subQ2=sQuery(id+"F2.wireOp",EDGE,"E21");var subQ3=sQuery(id+"F2.wireOp",EDGE,"E17");var subQ4=sQuery(id+"F0.wireOp",EDGE,"E6");Q8=makeQuery(id+"F15.boolean.opBoolean","MERGE",EDGE,{"derivedFrom":[makeQuery(id+"F3.opExtrude","SWEPT_EDGE",EDGE,{"disambiguationData":[OSD([subQ3,subQ2])]}),makeQuery(id+"F8.opExtrude","SWEPT_EDGE",EDGE,{"disambiguationData":[OSD([subQ4,subQ1,subQ0])]}),makeQuery(id+"F15.opExtrude","SWEPT_EDGE",EDGE,{"disambiguationData":[OSD([subQ4,subQ3,subQ2,subQ1,subQ0])]})]});}
            var Q9;
            {var subQ0=sQuery(id+"F7.wireOp",EDGE,"E23");var subQ1=sQuery(id+"F7.wireOp",EDGE,"E22");var subQ2=sQuery(id+"F2.wireOp",EDGE,"E20");var subQ3=sQuery(id+"F0.wireOp",EDGE,"E7");Q9=makeQuery(id+"F19.boolean.opBoolean","MERGE",EDGE,{"derivedFrom":[makeQuery(id+"F3.opExtrude","SWEPT_EDGE",EDGE,{"disambiguationData":[OSD([subQ3,subQ2])]}),makeQuery(id+"F8.opExtrude","SWEPT_EDGE",EDGE,{"disambiguationData":[OSD([subQ3,subQ1,subQ0])]}),makeQuery(id+"F19.opExtrude","SWEPT_EDGE",EDGE,{"disambiguationData":[OSD([subQ3,subQ2,subQ1,subQ0])]})]});}
            var Q10;
            {var subQ0=sQuery(id+"F7.wireOp",EDGE,"E24");var subQ1=sQuery(id+"F7.wireOp",EDGE,"E23");var subQ2=sQuery(id+"F2.wireOp",EDGE,"E21");var subQ3=sQuery(id+"F2.wireOp",EDGE,"E18");var subQ4=sQuery(id+"F0.wireOp",EDGE,"E6");Q10=makeQuery(id+"F15.boolean.opBoolean","MERGE",EDGE,{"derivedFrom":[makeQuery(id+"F3.opExtrude","SWEPT_EDGE",EDGE,{"disambiguationData":[OSD([subQ3,subQ2])]}),makeQuery(id+"F8.opExtrude","SWEPT_EDGE",EDGE,{"disambiguationData":[OSD([subQ4,subQ1,subQ0])]}),makeQuery(id+"F15.opExtrude","SWEPT_EDGE",EDGE,{"disambiguationData":[OSD([subQ4,subQ3,subQ2,subQ1,subQ0])]})]});}
            var Q11;
            {var subQ0=sQuery(id+"F13.wireOp",EDGE,"E35");var subQ1=sQuery(id+"F13.wireOp",EDGE,"E34");var subQ2=sQuery(id+"F2.wireOp",EDGE,"E21");var subQ3=sQuery(id+"F2.wireOp",EDGE,"E17");var subQ4=sQuery(id+"F0.wireOp",EDGE,"E6");Q11=makeQuery(id+"F15.boolean.opBoolean","MERGE",EDGE,{"derivedFrom":[makeQuery(id+"F4.opPattern","COPY",EDGE,{"derivedFrom":makeQuery(id+"F3.opExtrude","SWEPT_EDGE",EDGE,{"disambiguationData":[OSD([subQ3,subQ2])]}),"instanceName":"3"}),makeQuery(id+"F14.opExtrude","SWEPT_EDGE",EDGE,{"disambiguationData":[OSD([subQ4,subQ1,subQ0])]}),makeQuery(id+"F15.opExtrude","SWEPT_EDGE",EDGE,{"disambiguationData":[OSD([subQ4,subQ3,subQ2,subQ1,subQ0])]})]});}
            var Q12;
            {var subQ0=sQuery(id+"F13.wireOp",EDGE,"E37");var subQ1=sQuery(id+"F13.wireOp",EDGE,"E34");var subQ2=sQuery(id+"F2.wireOp",EDGE,"E21");var subQ3=sQuery(id+"F2.wireOp",EDGE,"E18");var subQ4=sQuery(id+"F0.wireOp",EDGE,"E6");Q12=makeQuery(id+"F15.boolean.opBoolean","MERGE",EDGE,{"derivedFrom":[makeQuery(id+"F4.opPattern","COPY",EDGE,{"derivedFrom":makeQuery(id+"F3.opExtrude","SWEPT_EDGE",EDGE,{"disambiguationData":[OSD([subQ3,subQ2])]}),"instanceName":"3"}),makeQuery(id+"F14.opExtrude","SWEPT_EDGE",EDGE,{"disambiguationData":[OSD([subQ4,subQ1,subQ0])]}),makeQuery(id+"F15.opExtrude","SWEPT_EDGE",EDGE,{"disambiguationData":[OSD([subQ4,subQ3,subQ2,subQ1,subQ0])]})]});}
            var Q13;
            {var subQ0=sQuery(id+"F13.wireOp",EDGE,"E36");var subQ1=sQuery(id+"F13.wireOp",EDGE,"E35");var subQ2=sQuery(id+"F2.wireOp",EDGE,"E19");var subQ3=sQuery(id+"F0.wireOp",EDGE,"E7");Q13=makeQuery(id+"F19.boolean.opBoolean","MERGE",EDGE,{"derivedFrom":[makeQuery(id+"F4.opPattern","COPY",EDGE,{"derivedFrom":makeQuery(id+"F3.opExtrude","SWEPT_EDGE",EDGE,{"disambiguationData":[OSD([subQ3,subQ2])]}),"instanceName":"3"}),makeQuery(id+"F14.opExtrude","SWEPT_EDGE",EDGE,{"disambiguationData":[OSD([subQ3,subQ1,subQ0])]}),makeQuery(id+"F19.opExtrude","SWEPT_EDGE",EDGE,{"disambiguationData":[OSD([subQ3,subQ2,subQ1,subQ0])]})]});}
            var Q14;
            {var subQ0=sQuery(id+"F13.wireOp",EDGE,"E37");var subQ1=sQuery(id+"F13.wireOp",EDGE,"E36");var subQ2=sQuery(id+"F2.wireOp",EDGE,"E20");var subQ3=sQuery(id+"F2.wireOp",EDGE,"E18");var subQ4=sQuery(id+"F0.wireOp",EDGE,"E11");var subQ5=sQuery(id+"F0.wireOp",EDGE,"E10");Q14=makeQuery(id+"F19.boolean.opBoolean","MERGE",EDGE,{"derivedFrom":[makeQuery(id+"F5.boolean.opBoolean","INTERSECT",EDGE,{"derivedFrom":[makeQuery(id+"F1.opExtrude","SWEPT_FACE",FACE,{"disambiguationData":[OSD([subQ5,subQ4])]}),makeQuery(id+"F4.opPattern","COPY",FACE,{"derivedFrom":makeQuery(id+"F3.opExtrude","SWEPT_FACE",FACE,{"disambiguationData":[OSD([subQ3,subQ2])]}),"instanceName":"3"}),makeQuery(id+"F5.opExtrude","SWEPT_FACE",FACE,{"disambiguationData":[OSD([subQ5,subQ4])]})]}),makeQuery(id+"F14.opExtrude","SWEPT_EDGE",EDGE,{"disambiguationData":[OSD([subQ5,subQ4,subQ1,subQ0])]}),makeQuery(id+"F19.opExtrude","SWEPT_EDGE",EDGE,{"disambiguationData":[OSD([subQ5,subQ4,subQ3,subQ2,subQ1,subQ0])]})]});}
            var Q15;
            {var subQ0=sQuery(id+"F11.wireOp",EDGE,"E32");var subQ1=sQuery(id+"F11.wireOp",EDGE,"E31");var subQ2=sQuery(id+"F2.wireOp",EDGE,"E19");var subQ3=sQuery(id+"F2.wireOp",EDGE,"E17");var subQ4=sQuery(id+"F0.wireOp",EDGE,"E11");var subQ5=sQuery(id+"F0.wireOp",EDGE,"E10");Q15=makeQuery(id+"F19.boolean.opBoolean","MERGE",EDGE,{"derivedFrom":[makeQuery(id+"F5.boolean.opBoolean","INTERSECT",EDGE,{"derivedFrom":[makeQuery(id+"F1.opExtrude","SWEPT_FACE",FACE,{"disambiguationData":[OSD([subQ5,subQ4])]}),makeQuery(id+"F4.opPattern","COPY",FACE,{"derivedFrom":makeQuery(id+"F3.opExtrude","SWEPT_FACE",FACE,{"disambiguationData":[OSD([subQ3,subQ2])]}),"instanceName":"2"}),makeQuery(id+"F5.opExtrude","SWEPT_FACE",FACE,{"disambiguationData":[OSD([subQ5,subQ4])]})]}),makeQuery(id+"F12.opExtrude","SWEPT_EDGE",EDGE,{"disambiguationData":[OSD([subQ5,subQ4,subQ1,subQ0])]}),makeQuery(id+"F19.opExtrude","SWEPT_EDGE",EDGE,{"disambiguationData":[OSD([subQ5,subQ4,subQ3,subQ2,subQ1,subQ0])]})]});}
            fillet(context, id + "F20", {"entities" : qUnion([Q0, Q1, Q2, Q3, Q4, Q5, Q6, Q7, Q8, Q9, Q10, Q11, Q12, Q13, Q14, Q15]), "radius" : 3 * mm, "tangentPropagation" : true, "allowEdgeOverflow" : false});
        }
        {
            var Q0;
            Q0=makeQuery(id+"F19.boolean.opBoolean","SPLIT",EDGE,{"derivedFrom":makeQuery(id+"F10.opExtrude","SWEPT_EDGE",EDGE,{"disambiguationData":[OSD([sQuery(id+"F0.wireOp",EDGE,"E7"),sQuery(id+"F9.wireOp",EDGE,"E27"),sQuery(id+"F9.wireOp",EDGE,"E28")])]})});
            var Q1;
            Q1=makeQuery(id+"F19.boolean.opBoolean","SPLIT",EDGE,{"derivedFrom":makeQuery(id+"F10.opExtrude","SWEPT_EDGE",EDGE,{"disambiguationData":[OSD([sQuery(id+"F0.wireOp",EDGE,"E7"),sQuery(id+"F9.wireOp",EDGE,"E27"),sQuery(id+"F9.wireOp",EDGE,"E30")])]})});
            var Q2;
            Q2=makeQuery(id+"F19.boolean.opBoolean","SPLIT",EDGE,{"derivedFrom":makeQuery(id+"F8.opExtrude","SWEPT_EDGE",EDGE,{"disambiguationData":[OSD([sQuery(id+"F0.wireOp",EDGE,"E7"),sQuery(id+"F7.wireOp",EDGE,"E22"),sQuery(id+"F7.wireOp",EDGE,"E25")])]})});
            var Q3;
            Q3=makeQuery(id+"F19.boolean.opBoolean","SPLIT",EDGE,{"derivedFrom":makeQuery(id+"F8.opExtrude","SWEPT_EDGE",EDGE,{"disambiguationData":[OSD([sQuery(id+"F0.wireOp",EDGE,"E7"),sQuery(id+"F7.wireOp",EDGE,"E22"),sQuery(id+"F7.wireOp",EDGE,"E23")])]})});
            var Q4;
            Q4=makeQuery(id+"F19.boolean.opBoolean","SPLIT",EDGE,{"derivedFrom":makeQuery(id+"F14.opExtrude","SWEPT_EDGE",EDGE,{"disambiguationData":[OSD([sQuery(id+"F0.wireOp",EDGE,"E7"),sQuery(id+"F13.wireOp",EDGE,"E35"),sQuery(id+"F13.wireOp",EDGE,"E36")])]})});
            var Q5;
            Q5=makeQuery(id+"F19.boolean.opBoolean","SPLIT",EDGE,{"derivedFrom":makeQuery(id+"F14.opExtrude","SWEPT_EDGE",EDGE,{"disambiguationData":[OSD([sQuery(id+"F0.wireOp",EDGE,"E10"),sQuery(id+"F0.wireOp",EDGE,"E11"),sQuery(id+"F13.wireOp",EDGE,"E36"),sQuery(id+"F13.wireOp",EDGE,"E37")])]})});
            fillet(context, id + "F21", {"entities" : qUnion([Q0, Q1, Q2, Q3, Q4, Q5]), "radius" : 2.5 * mm, "tangentPropagation" : true, "allowEdgeOverflow" : false});
        }
    });
